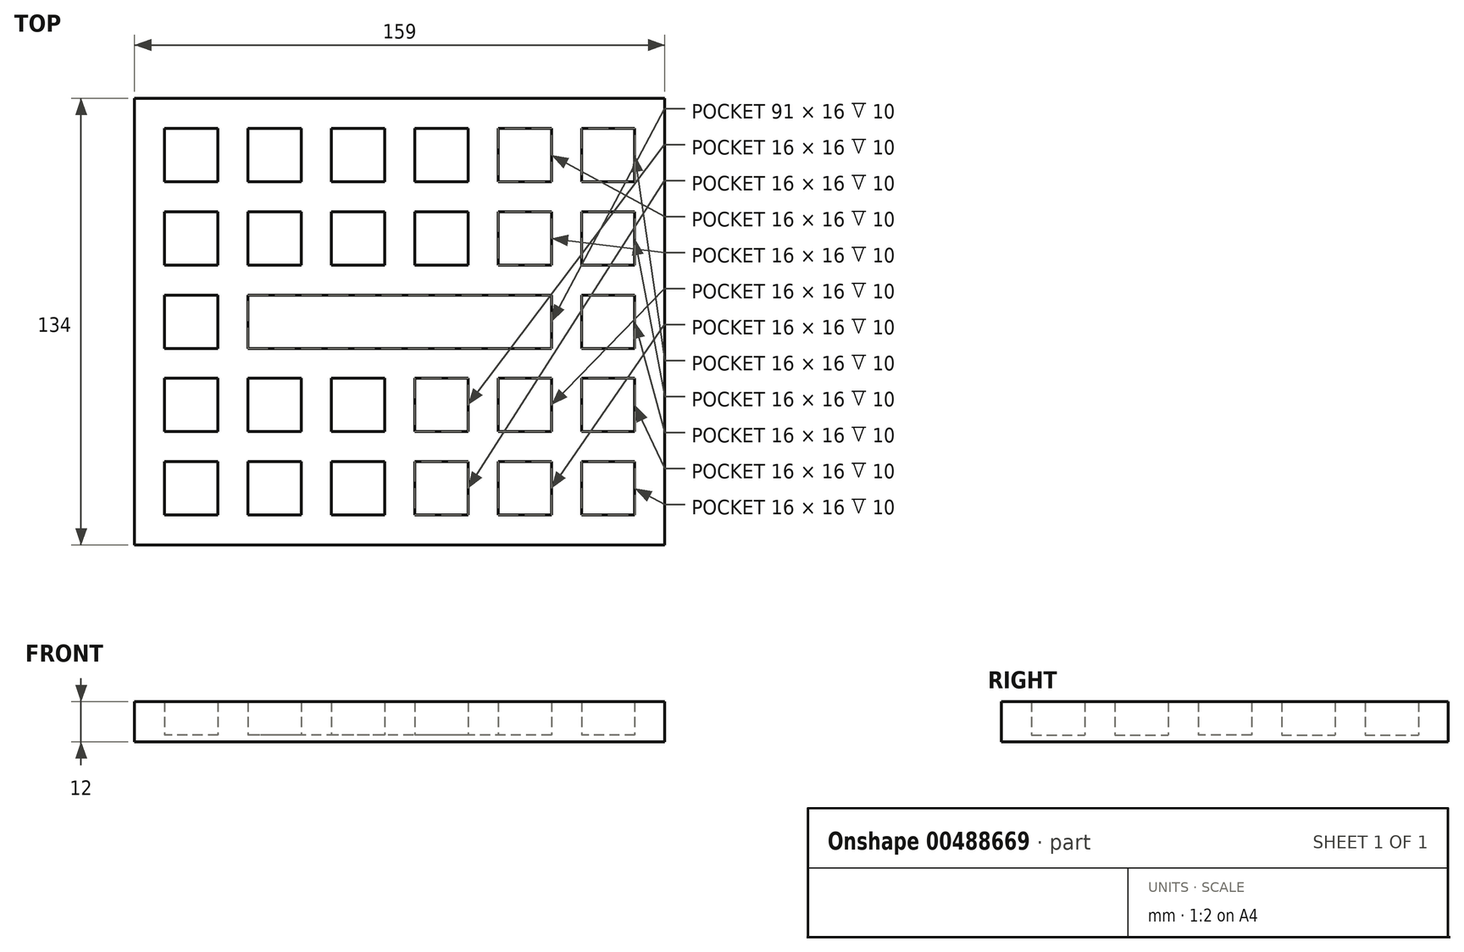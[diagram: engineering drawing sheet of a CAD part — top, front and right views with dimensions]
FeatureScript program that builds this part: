
annotation { "Feature Type Name" : "Feature", "Feature Type Description" : "" }
export const myFeature = defineFeature(function(context is Context, id is Id, definition is map)
    precondition{}
    {
        {
            var Q0;
            Q0=qCreatedBy(makeId("Top.planeOp"),FACE);
            var sketch = newSketch(context, id + "F0", { "sketchPlane" : qUnion([Q0])});
            skLineSegment(sketch, "E0.bottom", {"start": v(-54.5, 42) * mm, "end": v(-70.5, 42) * mm});
            skLineSegment(sketch, "E0.top", {"start": v(-54.5, 58) * mm, "end": v(-70.5, 58) * mm});
            skLineSegment(sketch, "E0.left", {"start": v(-54.5, 42) * mm, "end": v(-54.5, 58) * mm});
            skLineSegment(sketch, "E0.right", {"start": v(-70.5, 42) * mm, "end": v(-70.5, 58) * mm});
            skPoint(sketch, "E0.middle", {"position": v(-62.5, 50) * mm});
            skLineSegment(sketch, "E1.0.1.0", {"start": v(-54.5, 33) * mm, "end": v(-70.5, 33) * mm});
            skLineSegment(sketch, "E1.0.1.1", {"start": v(-54.5, 17) * mm, "end": v(-54.5, 33) * mm});
            skLineSegment(sketch, "E1.0.1.2", {"start": v(-70.5, 17) * mm, "end": v(-70.5, 33) * mm});
            skPoint(sketch, "E1.0.1.3", {"position": v(-62.5, 25) * mm});
            skLineSegment(sketch, "E1.0.1.4", {"start": v(-54.5, 17) * mm, "end": v(-70.5, 17) * mm});
            skLineSegment(sketch, "E1.0.2.0", {"start": v(-54.5, 8) * mm, "end": v(-70.5, 8) * mm});
            skLineSegment(sketch, "E1.0.2.1", {"start": v(-54.5, -8) * mm, "end": v(-54.5, 8) * mm});
            skLineSegment(sketch, "E1.0.2.2", {"start": v(-70.5, -8) * mm, "end": v(-70.5, 8) * mm});
            skPoint(sketch, "E1.0.2.3", {"position": v(-62.5, 0) * mm});
            skLineSegment(sketch, "E1.0.2.4", {"start": v(-54.5, -8) * mm, "end": v(-70.5, -8) * mm});
            skLineSegment(sketch, "E1.0.3.0", {"start": v(-54.5, -17) * mm, "end": v(-70.5, -17) * mm});
            skLineSegment(sketch, "E1.0.3.1", {"start": v(-54.5, -33) * mm, "end": v(-54.5, -17) * mm});
            skLineSegment(sketch, "E1.0.3.2", {"start": v(-70.5, -33) * mm, "end": v(-70.5, -17) * mm});
            skPoint(sketch, "E1.0.3.3", {"position": v(-62.5, -25) * mm});
            skLineSegment(sketch, "E1.0.3.4", {"start": v(-54.5, -33) * mm, "end": v(-70.5, -33) * mm});
            skLineSegment(sketch, "E1.0.4.0", {"start": v(-54.5, -42) * mm, "end": v(-70.5, -42) * mm});
            skLineSegment(sketch, "E1.0.4.1", {"start": v(-54.5, -58) * mm, "end": v(-54.5, -42) * mm});
            skLineSegment(sketch, "E1.0.4.2", {"start": v(-70.5, -58) * mm, "end": v(-70.5, -42) * mm});
            skPoint(sketch, "E1.0.4.3", {"position": v(-62.5, -50) * mm});
            skLineSegment(sketch, "E1.0.4.4", {"start": v(-54.5, -58) * mm, "end": v(-70.5, -58) * mm});
            skLineSegment(sketch, "E1.1.0.0", {"start": v(-29.5, 58) * mm, "end": v(-45.5, 58) * mm});
            skLineSegment(sketch, "E1.1.0.1", {"start": v(-29.5, 42) * mm, "end": v(-29.5, 58) * mm});
            skLineSegment(sketch, "E1.1.0.2", {"start": v(-45.5, 42) * mm, "end": v(-45.5, 58) * mm});
            skPoint(sketch, "E1.1.0.3", {"position": v(-37.5, 50) * mm});
            skLineSegment(sketch, "E1.1.0.4", {"start": v(-29.5, 42) * mm, "end": v(-45.5, 42) * mm});
            skLineSegment(sketch, "E1.1.1.0", {"start": v(-29.5, 33) * mm, "end": v(-45.5, 33) * mm});
            skLineSegment(sketch, "E1.1.1.1", {"start": v(-29.5, 17) * mm, "end": v(-29.5, 33) * mm});
            skLineSegment(sketch, "E1.1.1.2", {"start": v(-45.5, 17) * mm, "end": v(-45.5, 33) * mm});
            skPoint(sketch, "E1.1.1.3", {"position": v(-37.5, 25) * mm});
            skLineSegment(sketch, "E1.1.1.4", {"start": v(-29.5, 17) * mm, "end": v(-45.5, 17) * mm});
            skLineSegment(sketch, "E1.1.3.0", {"start": v(-29.5, -17) * mm, "end": v(-45.5, -17) * mm});
            skLineSegment(sketch, "E1.1.3.1", {"start": v(-29.5, -33) * mm, "end": v(-29.5, -17) * mm});
            skLineSegment(sketch, "E1.1.3.2", {"start": v(-45.5, -33) * mm, "end": v(-45.5, -17) * mm});
            skPoint(sketch, "E1.1.3.3", {"position": v(-37.5, -25) * mm});
            skLineSegment(sketch, "E1.1.3.4", {"start": v(-29.5, -33) * mm, "end": v(-45.5, -33) * mm});
            skLineSegment(sketch, "E1.1.4.0", {"start": v(-29.5, -42) * mm, "end": v(-45.5, -42) * mm});
            skLineSegment(sketch, "E1.1.4.1", {"start": v(-29.5, -58) * mm, "end": v(-29.5, -42) * mm});
            skLineSegment(sketch, "E1.1.4.2", {"start": v(-45.5, -58) * mm, "end": v(-45.5, -42) * mm});
            skPoint(sketch, "E1.1.4.3", {"position": v(-37.5, -50) * mm});
            skLineSegment(sketch, "E1.1.4.4", {"start": v(-29.5, -58) * mm, "end": v(-45.5, -58) * mm});
            skLineSegment(sketch, "E1.2.0.0", {"start": v(-4.5, 58) * mm, "end": v(-20.5, 58) * mm});
            skLineSegment(sketch, "E1.2.0.1", {"start": v(-4.5, 42) * mm, "end": v(-4.5, 58) * mm});
            skLineSegment(sketch, "E1.2.0.2", {"start": v(-20.5, 42) * mm, "end": v(-20.5, 58) * mm});
            skPoint(sketch, "E1.2.0.3", {"position": v(-12.5, 50) * mm});
            skLineSegment(sketch, "E1.2.0.4", {"start": v(-4.5, 42) * mm, "end": v(-20.5, 42) * mm});
            skLineSegment(sketch, "E1.2.1.0", {"start": v(-4.5, 33) * mm, "end": v(-20.5, 33) * mm});
            skLineSegment(sketch, "E1.2.1.1", {"start": v(-4.5, 17) * mm, "end": v(-4.5, 33) * mm});
            skLineSegment(sketch, "E1.2.1.2", {"start": v(-20.5, 17) * mm, "end": v(-20.5, 33) * mm});
            skPoint(sketch, "E1.2.1.3", {"position": v(-12.5, 25) * mm});
            skLineSegment(sketch, "E1.2.1.4", {"start": v(-4.5, 17) * mm, "end": v(-20.5, 17) * mm});
            skLineSegment(sketch, "E1.2.3.0", {"start": v(-4.5, -17) * mm, "end": v(-20.5, -17) * mm});
            skLineSegment(sketch, "E1.2.3.1", {"start": v(-4.5, -33) * mm, "end": v(-4.5, -17) * mm});
            skLineSegment(sketch, "E1.2.3.2", {"start": v(-20.5, -33) * mm, "end": v(-20.5, -17) * mm});
            skPoint(sketch, "E1.2.3.3", {"position": v(-12.5, -25) * mm});
            skLineSegment(sketch, "E1.2.3.4", {"start": v(-4.5, -33) * mm, "end": v(-20.5, -33) * mm});
            skLineSegment(sketch, "E1.2.4.0", {"start": v(-4.5, -42) * mm, "end": v(-20.5, -42) * mm});
            skLineSegment(sketch, "E1.2.4.1", {"start": v(-4.5, -58) * mm, "end": v(-4.5, -42) * mm});
            skLineSegment(sketch, "E1.2.4.2", {"start": v(-20.5, -58) * mm, "end": v(-20.5, -42) * mm});
            skPoint(sketch, "E1.2.4.3", {"position": v(-12.5, -50) * mm});
            skLineSegment(sketch, "E1.2.4.4", {"start": v(-4.5, -58) * mm, "end": v(-20.5, -58) * mm});
            skLineSegment(sketch, "E1.3.0.0", {"start": v(20.5, 58) * mm, "end": v(4.5, 58) * mm});
            skLineSegment(sketch, "E1.3.0.1", {"start": v(20.5, 42) * mm, "end": v(20.5, 58) * mm});
            skLineSegment(sketch, "E1.3.0.2", {"start": v(4.5, 42) * mm, "end": v(4.5, 58) * mm});
            skPoint(sketch, "E1.3.0.3", {"position": v(12.5, 50) * mm});
            skLineSegment(sketch, "E1.3.0.4", {"start": v(20.5, 42) * mm, "end": v(4.5, 42) * mm});
            skLineSegment(sketch, "E1.3.1.0", {"start": v(20.5, 33) * mm, "end": v(4.5, 33) * mm});
            skLineSegment(sketch, "E1.3.1.1", {"start": v(20.5, 17) * mm, "end": v(20.5, 33) * mm});
            skLineSegment(sketch, "E1.3.1.2", {"start": v(4.5, 17) * mm, "end": v(4.5, 33) * mm});
            skPoint(sketch, "E1.3.1.3", {"position": v(12.5, 25) * mm});
            skLineSegment(sketch, "E1.3.1.4", {"start": v(20.5, 17) * mm, "end": v(4.5, 17) * mm});
            skLineSegment(sketch, "E1.3.3.0", {"start": v(20.5, -17) * mm, "end": v(4.5, -17) * mm});
            skLineSegment(sketch, "E1.3.3.1", {"start": v(20.5, -33) * mm, "end": v(20.5, -17) * mm});
            skLineSegment(sketch, "E1.3.3.2", {"start": v(4.5, -33) * mm, "end": v(4.5, -17) * mm});
            skPoint(sketch, "E1.3.3.3", {"position": v(12.5, -25) * mm});
            skLineSegment(sketch, "E1.3.3.4", {"start": v(20.5, -33) * mm, "end": v(4.5, -33) * mm});
            skLineSegment(sketch, "E1.3.4.0", {"start": v(20.5, -42) * mm, "end": v(4.5, -42) * mm});
            skLineSegment(sketch, "E1.3.4.1", {"start": v(20.5, -58) * mm, "end": v(20.5, -42) * mm});
            skLineSegment(sketch, "E1.3.4.2", {"start": v(4.5, -58) * mm, "end": v(4.5, -42) * mm});
            skPoint(sketch, "E1.3.4.3", {"position": v(12.5, -50) * mm});
            skLineSegment(sketch, "E1.3.4.4", {"start": v(20.5, -58) * mm, "end": v(4.5, -58) * mm});
            skLineSegment(sketch, "E1.4.0.0", {"start": v(45.5, 58) * mm, "end": v(29.5, 58) * mm});
            skLineSegment(sketch, "E1.4.0.1", {"start": v(45.5, 42) * mm, "end": v(45.5, 58) * mm});
            skLineSegment(sketch, "E1.4.0.2", {"start": v(29.5, 42) * mm, "end": v(29.5, 58) * mm});
            skPoint(sketch, "E1.4.0.3", {"position": v(37.5, 50) * mm});
            skLineSegment(sketch, "E1.4.0.4", {"start": v(45.5, 42) * mm, "end": v(29.5, 42) * mm});
            skLineSegment(sketch, "E1.4.1.0", {"start": v(45.5, 33) * mm, "end": v(29.5, 33) * mm});
            skLineSegment(sketch, "E1.4.1.1", {"start": v(45.5, 17) * mm, "end": v(45.5, 33) * mm});
            skLineSegment(sketch, "E1.4.1.2", {"start": v(29.5, 17) * mm, "end": v(29.5, 33) * mm});
            skPoint(sketch, "E1.4.1.3", {"position": v(37.5, 25) * mm});
            skLineSegment(sketch, "E1.4.1.4", {"start": v(45.5, 17) * mm, "end": v(29.5, 17) * mm});
            skLineSegment(sketch, "E1.4.3.0", {"start": v(45.5, -17) * mm, "end": v(29.5, -17) * mm});
            skLineSegment(sketch, "E1.4.3.1", {"start": v(45.5, -33) * mm, "end": v(45.5, -17) * mm});
            skLineSegment(sketch, "E1.4.3.2", {"start": v(29.5, -33) * mm, "end": v(29.5, -17) * mm});
            skPoint(sketch, "E1.4.3.3", {"position": v(37.5, -25) * mm});
            skLineSegment(sketch, "E1.4.3.4", {"start": v(45.5, -33) * mm, "end": v(29.5, -33) * mm});
            skLineSegment(sketch, "E1.4.4.0", {"start": v(45.5, -42) * mm, "end": v(29.5, -42) * mm});
            skLineSegment(sketch, "E1.4.4.1", {"start": v(45.5, -58) * mm, "end": v(45.5, -42) * mm});
            skLineSegment(sketch, "E1.4.4.2", {"start": v(29.5, -58) * mm, "end": v(29.5, -42) * mm});
            skPoint(sketch, "E1.4.4.3", {"position": v(37.5, -50) * mm});
            skLineSegment(sketch, "E1.4.4.4", {"start": v(45.5, -58) * mm, "end": v(29.5, -58) * mm});
            skLineSegment(sketch, "E1.5.0.0", {"start": v(70.5, 58) * mm, "end": v(54.5, 58) * mm});
            skLineSegment(sketch, "E1.5.0.1", {"start": v(70.5, 42) * mm, "end": v(70.5, 58) * mm});
            skLineSegment(sketch, "E1.5.0.2", {"start": v(54.5, 42) * mm, "end": v(54.5, 58) * mm});
            skPoint(sketch, "E1.5.0.3", {"position": v(62.5, 50) * mm});
            skLineSegment(sketch, "E1.5.0.4", {"start": v(70.5, 42) * mm, "end": v(54.5, 42) * mm});
            skLineSegment(sketch, "E1.5.1.0", {"start": v(70.5, 33) * mm, "end": v(54.5, 33) * mm});
            skLineSegment(sketch, "E1.5.1.1", {"start": v(70.5, 17) * mm, "end": v(70.5, 33) * mm});
            skLineSegment(sketch, "E1.5.1.2", {"start": v(54.5, 17) * mm, "end": v(54.5, 33) * mm});
            skPoint(sketch, "E1.5.1.3", {"position": v(62.5, 25) * mm});
            skLineSegment(sketch, "E1.5.1.4", {"start": v(70.5, 17) * mm, "end": v(54.5, 17) * mm});
            skLineSegment(sketch, "E1.5.2.0", {"start": v(70.5, 8) * mm, "end": v(54.5, 8) * mm});
            skLineSegment(sketch, "E1.5.2.1", {"start": v(70.5, -8) * mm, "end": v(70.5, 8) * mm});
            skLineSegment(sketch, "E1.5.2.2", {"start": v(54.5, -8) * mm, "end": v(54.5, 8) * mm});
            skPoint(sketch, "E1.5.2.3", {"position": v(62.5, 0) * mm});
            skLineSegment(sketch, "E1.5.2.4", {"start": v(70.5, -8) * mm, "end": v(54.5, -8) * mm});
            skLineSegment(sketch, "E1.5.3.0", {"start": v(70.5, -17) * mm, "end": v(54.5, -17) * mm});
            skLineSegment(sketch, "E1.5.3.1", {"start": v(70.5, -33) * mm, "end": v(70.5, -17) * mm});
            skLineSegment(sketch, "E1.5.3.2", {"start": v(54.5, -33) * mm, "end": v(54.5, -17) * mm});
            skPoint(sketch, "E1.5.3.3", {"position": v(62.5, -25) * mm});
            skLineSegment(sketch, "E1.5.3.4", {"start": v(70.5, -33) * mm, "end": v(54.5, -33) * mm});
            skLineSegment(sketch, "E1.5.4.0", {"start": v(70.5, -42) * mm, "end": v(54.5, -42) * mm});
            skLineSegment(sketch, "E1.5.4.1", {"start": v(70.5, -58) * mm, "end": v(70.5, -42) * mm});
            skLineSegment(sketch, "E1.5.4.2", {"start": v(54.5, -58) * mm, "end": v(54.5, -42) * mm});
            skPoint(sketch, "E1.5.4.3", {"position": v(62.5, -50) * mm});
            skLineSegment(sketch, "E1.5.4.4", {"start": v(70.5, -58) * mm, "end": v(54.5, -58) * mm});
            skLineSegment(sketch, "E1.direction1", {"start": v(-70.5, 42) * mm, "end": v(-45.5, 42) * mm, "construction": true});
            skLineSegment(sketch, "E1.direction2", {"start": v(-70.5, 42) * mm, "end": v(-70.5, 17) * mm, "construction": true});
            skLineSegment(sketch, "E2", {"start": v(-54.5, 0) * mm, "end": v(54.5, 0) * mm, "construction": true});
            skLineSegment(sketch, "E3.bottom", {"start": v(45.5, 8) * mm, "end": v(-45.5, 8) * mm});
            skLineSegment(sketch, "E3.top", {"start": v(45.5, -8) * mm, "end": v(-45.5, -8) * mm});
            skLineSegment(sketch, "E3.left", {"start": v(45.5, 8) * mm, "end": v(45.5, -8) * mm});
            skLineSegment(sketch, "E3.right", {"start": v(-45.5, 8) * mm, "end": v(-45.5, -8) * mm});
            skPoint(sketch, "E3.middle", {"position": v(0, 0) * mm});
            skLineSegment(sketch, "E4.bottom", {"start": v(79.5, 67) * mm, "end": v(-79.5, 67) * mm});
            skLineSegment(sketch, "E4.top", {"start": v(79.5, -67) * mm, "end": v(-79.5, -67) * mm});
            skLineSegment(sketch, "E4.left", {"start": v(79.5, 67) * mm, "end": v(79.5, -67) * mm});
            skLineSegment(sketch, "E4.right", {"start": v(-79.5, 67) * mm, "end": v(-79.5, -67) * mm});
            skSolve(sketch);
        }
        {
            var Q0;
            Q0 = qSketchRegion(id + "F0", true);
            extrude(context, id + "F1", {"entities" : qUnion([Q0]), "depth" : 10 * mm});
        }
        {
            var Q0;
            Q0=makeQuery(id+"F1.opExtrude","CAP_FACE",FACE,{"disambiguationData":[OSD([sQuery(id+"F0.wireOp",EDGE,"E0.bottom"),sQuery(id+"F0.wireOp",EDGE,"E0.top"),sQuery(id+"F0.wireOp",EDGE,"E0.left"),sQuery(id+"F0.wireOp",EDGE,"E0.right"),sQuery(id+"F0.wireOp",EDGE,"E1.0.1.0"),sQuery(id+"F0.wireOp",EDGE,"E1.0.1.1"),sQuery(id+"F0.wireOp",EDGE,"E1.0.1.2"),sQuery(id+"F0.wireOp",EDGE,"E1.0.1.4"),sQuery(id+"F0.wireOp",EDGE,"E1.0.2.0"),sQuery(id+"F0.wireOp",EDGE,"E1.0.2.1"),sQuery(id+"F0.wireOp",EDGE,"E1.0.2.2"),sQuery(id+"F0.wireOp",EDGE,"E1.0.2.4"),sQuery(id+"F0.wireOp",EDGE,"E1.0.3.0"),sQuery(id+"F0.wireOp",EDGE,"E1.0.3.1"),sQuery(id+"F0.wireOp",EDGE,"E1.0.3.2"),sQuery(id+"F0.wireOp",EDGE,"E1.0.3.4"),sQuery(id+"F0.wireOp",EDGE,"E1.0.4.0"),sQuery(id+"F0.wireOp",EDGE,"E1.0.4.1"),sQuery(id+"F0.wireOp",EDGE,"E1.0.4.2"),sQuery(id+"F0.wireOp",EDGE,"E1.0.4.4"),sQuery(id+"F0.wireOp",EDGE,"E1.1.0.0"),sQuery(id+"F0.wireOp",EDGE,"E1.1.0.1"),sQuery(id+"F0.wireOp",EDGE,"E1.1.0.2"),sQuery(id+"F0.wireOp",EDGE,"E1.1.0.4"),sQuery(id+"F0.wireOp",EDGE,"E1.1.1.0"),sQuery(id+"F0.wireOp",EDGE,"E1.1.1.1"),sQuery(id+"F0.wireOp",EDGE,"E1.1.1.2"),sQuery(id+"F0.wireOp",EDGE,"E1.1.1.4"),sQuery(id+"F0.wireOp",EDGE,"E1.1.3.0"),sQuery(id+"F0.wireOp",EDGE,"E1.1.3.1"),sQuery(id+"F0.wireOp",EDGE,"E1.1.3.2"),sQuery(id+"F0.wireOp",EDGE,"E1.1.3.4"),sQuery(id+"F0.wireOp",EDGE,"E1.1.4.0"),sQuery(id+"F0.wireOp",EDGE,"E1.1.4.1"),sQuery(id+"F0.wireOp",EDGE,"E1.1.4.2"),sQuery(id+"F0.wireOp",EDGE,"E1.1.4.4"),sQuery(id+"F0.wireOp",EDGE,"E1.2.0.0"),sQuery(id+"F0.wireOp",EDGE,"E1.2.0.1"),sQuery(id+"F0.wireOp",EDGE,"E1.2.0.2"),sQuery(id+"F0.wireOp",EDGE,"E1.2.0.4"),sQuery(id+"F0.wireOp",EDGE,"E1.2.1.0"),sQuery(id+"F0.wireOp",EDGE,"E1.2.1.1"),sQuery(id+"F0.wireOp",EDGE,"E1.2.1.2"),sQuery(id+"F0.wireOp",EDGE,"E1.2.1.4"),sQuery(id+"F0.wireOp",EDGE,"E1.2.3.0"),sQuery(id+"F0.wireOp",EDGE,"E1.2.3.1"),sQuery(id+"F0.wireOp",EDGE,"E1.2.3.2"),sQuery(id+"F0.wireOp",EDGE,"E1.2.3.4"),sQuery(id+"F0.wireOp",EDGE,"E1.2.4.0"),sQuery(id+"F0.wireOp",EDGE,"E1.2.4.1"),sQuery(id+"F0.wireOp",EDGE,"E1.2.4.2"),sQuery(id+"F0.wireOp",EDGE,"E1.2.4.4"),sQuery(id+"F0.wireOp",EDGE,"E1.3.0.0"),sQuery(id+"F0.wireOp",EDGE,"E1.3.0.1"),sQuery(id+"F0.wireOp",EDGE,"E1.3.0.2"),sQuery(id+"F0.wireOp",EDGE,"E1.3.0.4"),sQuery(id+"F0.wireOp",EDGE,"E1.3.1.0"),sQuery(id+"F0.wireOp",EDGE,"E1.3.1.1"),sQuery(id+"F0.wireOp",EDGE,"E1.3.1.2"),sQuery(id+"F0.wireOp",EDGE,"E1.3.1.4"),sQuery(id+"F0.wireOp",EDGE,"E1.3.3.0"),sQuery(id+"F0.wireOp",EDGE,"E1.3.3.1"),sQuery(id+"F0.wireOp",EDGE,"E1.3.3.2"),sQuery(id+"F0.wireOp",EDGE,"E1.3.3.4"),sQuery(id+"F0.wireOp",EDGE,"E1.3.4.0"),sQuery(id+"F0.wireOp",EDGE,"E1.3.4.1"),sQuery(id+"F0.wireOp",EDGE,"E1.3.4.2"),sQuery(id+"F0.wireOp",EDGE,"E1.3.4.4"),sQuery(id+"F0.wireOp",EDGE,"E1.4.0.0"),sQuery(id+"F0.wireOp",EDGE,"E1.4.0.1"),sQuery(id+"F0.wireOp",EDGE,"E1.4.0.2"),sQuery(id+"F0.wireOp",EDGE,"E1.4.0.4"),sQuery(id+"F0.wireOp",EDGE,"E1.4.1.0"),sQuery(id+"F0.wireOp",EDGE,"E1.4.1.1"),sQuery(id+"F0.wireOp",EDGE,"E1.4.1.2"),sQuery(id+"F0.wireOp",EDGE,"E1.4.1.4"),sQuery(id+"F0.wireOp",EDGE,"E1.4.3.0"),sQuery(id+"F0.wireOp",EDGE,"E1.4.3.1"),sQuery(id+"F0.wireOp",EDGE,"E1.4.3.2"),sQuery(id+"F0.wireOp",EDGE,"E1.4.3.4"),sQuery(id+"F0.wireOp",EDGE,"E1.4.4.0"),sQuery(id+"F0.wireOp",EDGE,"E1.4.4.1"),sQuery(id+"F0.wireOp",EDGE,"E1.4.4.2"),sQuery(id+"F0.wireOp",EDGE,"E1.4.4.4"),sQuery(id+"F0.wireOp",EDGE,"E1.5.0.0"),sQuery(id+"F0.wireOp",EDGE,"E1.5.0.1"),sQuery(id+"F0.wireOp",EDGE,"E1.5.0.2"),sQuery(id+"F0.wireOp",EDGE,"E1.5.0.4"),sQuery(id+"F0.wireOp",EDGE,"E1.5.1.0"),sQuery(id+"F0.wireOp",EDGE,"E1.5.1.1"),sQuery(id+"F0.wireOp",EDGE,"E1.5.1.2"),sQuery(id+"F0.wireOp",EDGE,"E1.5.1.4"),sQuery(id+"F0.wireOp",EDGE,"E1.5.2.0"),sQuery(id+"F0.wireOp",EDGE,"E1.5.2.1"),sQuery(id+"F0.wireOp",EDGE,"E1.5.2.2"),sQuery(id+"F0.wireOp",EDGE,"E1.5.2.4"),sQuery(id+"F0.wireOp",EDGE,"E1.5.3.0"),sQuery(id+"F0.wireOp",EDGE,"E1.5.3.1"),sQuery(id+"F0.wireOp",EDGE,"E1.5.3.2"),sQuery(id+"F0.wireOp",EDGE,"E1.5.3.4"),sQuery(id+"F0.wireOp",EDGE,"E1.5.4.0"),sQuery(id+"F0.wireOp",EDGE,"E1.5.4.1"),sQuery(id+"F0.wireOp",EDGE,"E1.5.4.2"),sQuery(id+"F0.wireOp",EDGE,"E1.5.4.4"),sQuery(id+"F0.wireOp",EDGE,"E3.bottom"),sQuery(id+"F0.wireOp",EDGE,"E3.top"),sQuery(id+"F0.wireOp",EDGE,"E3.left"),sQuery(id+"F0.wireOp",EDGE,"E3.right"),sQuery(id+"F0.wireOp",EDGE,"E4.bottom"),sQuery(id+"F0.wireOp",EDGE,"E4.top"),sQuery(id+"F0.wireOp",EDGE,"E4.left"),sQuery(id+"F0.wireOp",EDGE,"E4.right")])],"isStart":true});
            var sketch = newSketch(context, id + "F2", { "sketchPlane" : qUnion([Q0])});
            skLineSegment(sketch, "E5.bottom", {"start": v(79.5, 67) * mm, "end": v(-79.5, 67) * mm});
            skLineSegment(sketch, "E5.top", {"start": v(79.5, -67) * mm, "end": v(-79.5, -67) * mm});
            skLineSegment(sketch, "E5.left", {"start": v(79.5, 67) * mm, "end": v(79.5, -67) * mm});
            skLineSegment(sketch, "E5.right", {"start": v(-79.5, 67) * mm, "end": v(-79.5, -67) * mm});
            skSolve(sketch);
        }
        {
            var Q0;
            Q0 = qSketchRegion(id + "F2", true);
            extrude(context, id + "F3", {"entities" : qUnion([Q0]), "operationType" : NewBodyOperationType.ADD, "depth" : 2 * mm});
        }
    });
